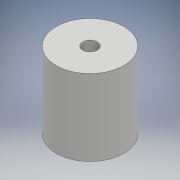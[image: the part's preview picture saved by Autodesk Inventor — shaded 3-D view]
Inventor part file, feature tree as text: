
AUTODESK INVENTOR PART (.ipt)
format: ipt  version: 2017 (Build 210142000, 142)  size: 206,848 bytes
history: native  units: mm
features: extrude x1, sketch x1
ambient origin geometry x8: Origin, YZ Plane, XZ Plane, XY Plane, X Axis, Y Axis, Z Axis, Center Point
bodies: Solid1 (feature_tree)
feature tree (2):
  extrude  "Extrusion1"  Depth=23.0mm
  sketch  "Sketch1"  dims[d0=20.4mm d1=4.4mm d2=23.0mm d3=0.0mm]
